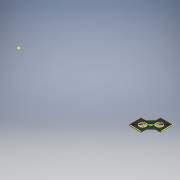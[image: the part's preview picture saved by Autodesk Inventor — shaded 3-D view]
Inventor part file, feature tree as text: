
AUTODESK INVENTOR PART (.ipt)
format: ipt  version: 2018 (Build 220112000, 112)  size: 1,027,584 bytes
history: native  units: mm
features: sketch x6, extrude x5, other x2, fillet x1
ambient origin geometry x8: Origin, YZ Plane, XZ Plane, XY Plane, X Axis, Y Axis, Z Axis, Center Point
bodies: Solid1 (feature_tree)
feature tree (14):
  other  "31.5mm_Driven_Element"
  other  "MeshFeature1"
  extrude  "Extrusion1"  Depth=19.0mm
  extrude  "Extrusion2"  Depth=22.0mm
  extrude  "Extrusion3"  Depth=2.6mm TaperAngle=0.0deg
  extrude  "Extrusion6"  Depth=31.5mm
  extrude  "Extrusion7"  Depth=27.9mm
  fillet  "Fillet2"  Radius=27.9mm
  sketch  "Sketch10"  dims[d21=27.9mm d22=27.9mm d23=1.8mm d24=0.0mm d29=1.8mm d32=2.62mm d33=0.0mm d34=10.0mm d35=2.62mm d36=0.0mm d37=0.5mm]
  sketch  "Sketch1"  dims[d0=19.0mm d1=19.0mm]
  sketch  "Sketch2"  dims[d2=22.0mm d3=22.0mm]
  sketch  "Sketch3"  dims[d4=2.62mm d5=0.0mm d6=2.6mm d7=0.0mm]
  sketch  "Sketch8"  dims[d15=31.5mm d16=31.5mm]
  sketch  "Sketch9"  dims[d17=31.5mm d19=27.9mm d20=27.9mm]
